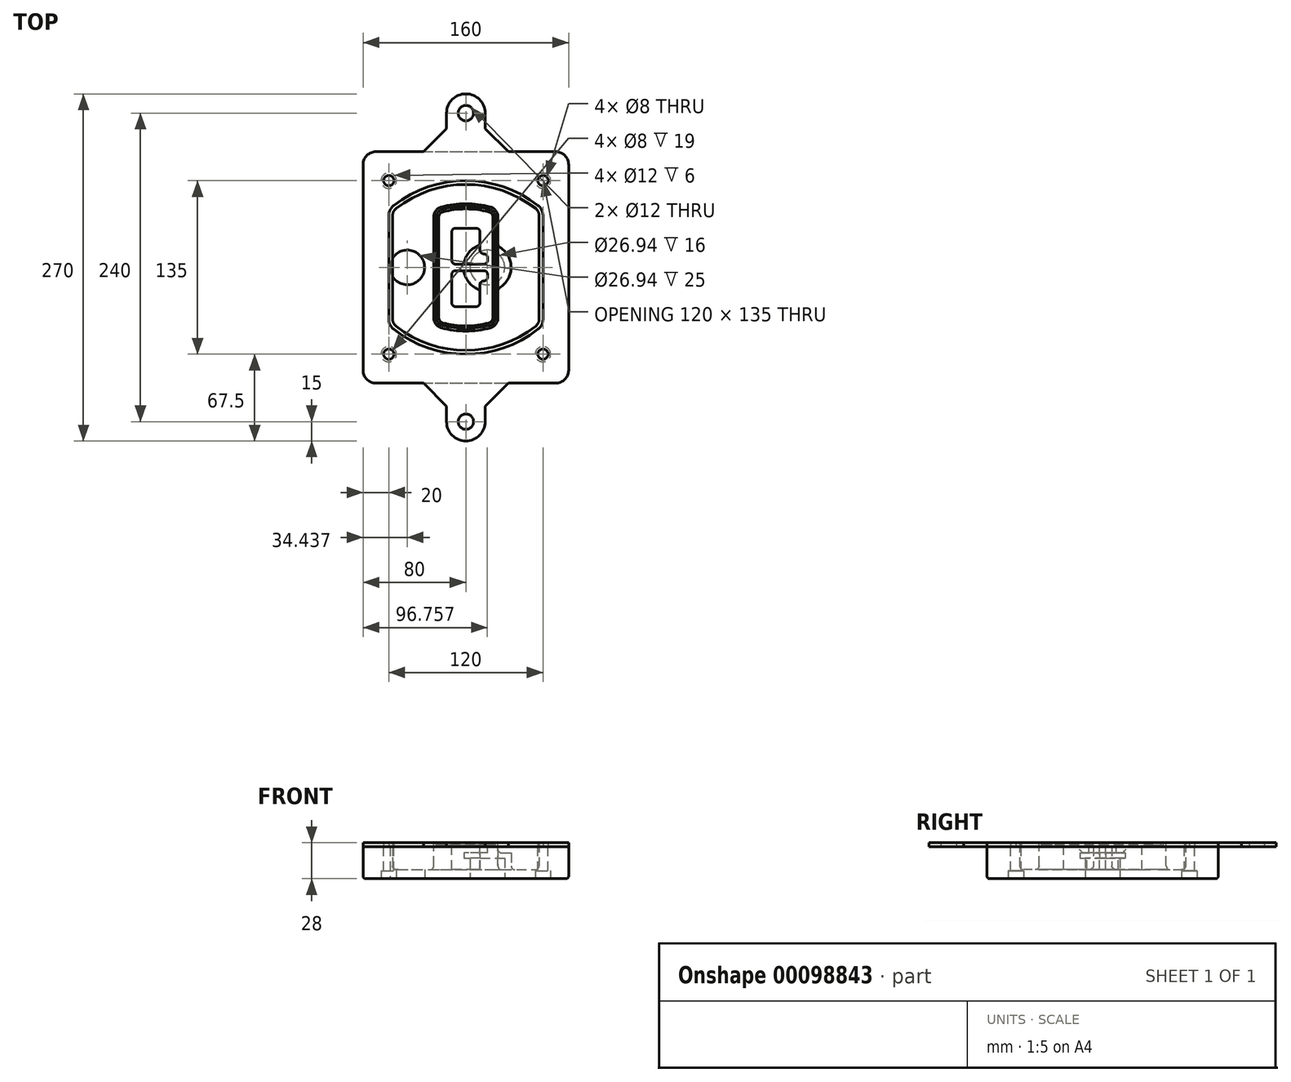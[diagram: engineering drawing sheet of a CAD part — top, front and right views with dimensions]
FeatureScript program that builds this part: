
annotation { "Feature Type Name" : "Feature", "Feature Type Description" : "" }
export const myFeature = defineFeature(function(context is Context, id is Id, definition is map)
    precondition{}
    {
        {
            var Q0;
            Q0=qCreatedBy(makeId("Top.planeOp"),FACE);
            var sketch = newSketch(context, id + "F0", { "sketchPlane" : qUnion([Q0])});
            skPoint(sketch, "E0.rect.middle", {"position": v(0, 0) * mm});
            skLineSegment(sketch, "E1.bottom", {"start": v(-70, -90) * mm, "end": v(70, -90) * mm});
            skLineSegment(sketch, "E1.top", {"start": v(-70, 90) * mm, "end": v(70, 90) * mm});
            skLineSegment(sketch, "E1.left", {"start": v(-80, -80) * mm, "end": v(-80, 80) * mm});
            skLineSegment(sketch, "E1.right", {"start": v(80, -80) * mm, "end": v(80, 80) * mm});
            skLineSegment(sketch, "E2", {"start": v(-80, 90) * mm, "end": v(80, -90) * mm, "construction": true});
            skLineSegment(sketch, "E3", {"start": v(80, 90) * mm, "end": v(-80, -90) * mm, "construction": true});
            skCircle(sketch, "E4", {"center": v(-60, 67.5) * mm, "radius": 4 * mm});
            skCircle(sketch, "E5", {"center": v(60, 67.5) * mm, "radius": 4 * mm});
            skCircle(sketch, "E6", {"center": v(60, -67.5) * mm, "radius": 4 * mm});
            skCircle(sketch, "E7", {"center": v(-60, -67.5) * mm, "radius": 4 * mm});
            skLineSegment(sketch, "E8", {"start": v(-60, 67.5) * mm, "end": v(60, 67.5) * mm, "construction": true});
            skLineSegment(sketch, "E9", {"start": v(60, 67.5) * mm, "end": v(60, -67.5) * mm, "construction": true});
            skLineSegment(sketch, "E10", {"start": v(60, -67.5) * mm, "end": v(-60, -67.5) * mm, "construction": true});
            skLineSegment(sketch, "E11", {"start": v(-60, -67.5) * mm, "end": v(-60, 67.5) * mm, "construction": true});
            skLineSegment(sketch, "E12", {"start": v(-60, 40.3) * mm, "end": v(-60, -40.3) * mm});
            skLineSegment(sketch, "E13", {"start": v(60, 40.3) * mm, "end": v(60, -40.3) * mm});
            skArc(sketch, "E14", {"start": v(56.15, 48.18) * mm, "mid": v(0, 67.5) * mm, "end": v(-56.15, 48.18) * mm});
            skArc(sketch, "E15", {"start": v(-56.15, -48.18) * mm, "mid": v(0, -67.5) * mm, "end": v(56.15, -48.18) * mm});
            skLineSegment(sketch, "E16", {"start": v(-60, 0) * mm, "end": v(60, 0) * mm, "construction": true});
            skPoint(sketch, "E17.visualSharp", {"position": v(-60, -45) * mm});
            skArc(sketch, "E17.filletArc", {"start": v(-60, -40.3) * mm, "mid": v(-58.99, -44.68) * mm, "end": v(-56.15, -48.18) * mm});
            skPoint(sketch, "E18.visualSharp", {"position": v(-60, 45) * mm});
            skArc(sketch, "E18.filletArc", {"start": v(-56.15, 48.18) * mm, "mid": v(-58.99, 44.68) * mm, "end": v(-60, 40.3) * mm});
            skPoint(sketch, "E19.visualSharp", {"position": v(60, 45) * mm});
            skArc(sketch, "E19.filletArc", {"start": v(60, 40.3) * mm, "mid": v(58.99, 44.68) * mm, "end": v(56.15, 48.18) * mm});
            skPoint(sketch, "E20.visualSharp", {"position": v(60, -45) * mm});
            skArc(sketch, "E20.filletArc", {"start": v(56.15, -48.18) * mm, "mid": v(58.99, -44.68) * mm, "end": v(60, -40.3) * mm});
            skPoint(sketch, "E21.visualSharp", {"position": v(-80, 90) * mm});
            skArc(sketch, "E21.filletArc", {"start": v(-70, 90) * mm, "mid": v(-77.07, 87.07) * mm, "end": v(-80, 80) * mm});
            skPoint(sketch, "E22.visualSharp", {"position": v(80, 90) * mm});
            skArc(sketch, "E22.filletArc", {"start": v(80, 80) * mm, "mid": v(77.07, 87.07) * mm, "end": v(70, 90) * mm});
            skPoint(sketch, "E23.visualSharp", {"position": v(80, -90) * mm});
            skArc(sketch, "E23.filletArc", {"start": v(70, -90) * mm, "mid": v(77.07, -87.07) * mm, "end": v(80, -80) * mm});
            skPoint(sketch, "E24.visualSharp", {"position": v(-80, -90) * mm});
            skArc(sketch, "E24.filletArc", {"start": v(-80, -80) * mm, "mid": v(-77.07, -87.07) * mm, "end": v(-70, -90) * mm});
            skArc(sketch, "E25.0", {"start": v(57, 40.3) * mm, "mid": v(56.3, 43.36) * mm, "end": v(54.3, 45.81) * mm});
            skLineSegment(sketch, "E25.1", {"start": v(57, 40.3) * mm, "end": v(57, -40.3) * mm});
            skArc(sketch, "E25.2", {"start": v(54.3, -45.81) * mm, "mid": v(56.3, -43.36) * mm, "end": v(57, -40.3) * mm});
            skArc(sketch, "E25.3", {"start": v(-54.3, -45.81) * mm, "mid": v(0, -64.5) * mm, "end": v(54.3, -45.81) * mm});
            skArc(sketch, "E25.4", {"start": v(-57, -40.3) * mm, "mid": v(-56.3, -43.36) * mm, "end": v(-54.3, -45.81) * mm});
            skArc(sketch, "E25.5", {"start": v(54.3, 45.81) * mm, "mid": v(0, 64.5) * mm, "end": v(-54.3, 45.81) * mm});
            skLineSegment(sketch, "E25.6", {"start": v(-57, 40.3) * mm, "end": v(-57, -40.3) * mm});
            skArc(sketch, "E25.7", {"start": v(-54.3, 45.81) * mm, "mid": v(-56.3, 43.36) * mm, "end": v(-57, 40.3) * mm});
            skArc(sketch, "E26.0", {"start": v(-58.62, 51.33) * mm, "mid": v(-62.58, 46.43) * mm, "end": v(-64, 40.3) * mm});
            skArc(sketch, "E26.1", {"start": v(58.62, 51.33) * mm, "mid": v(0, 71.5) * mm, "end": v(-58.62, 51.33) * mm});
            skArc(sketch, "E26.2", {"start": v(64, 40.3) * mm, "mid": v(62.58, 46.43) * mm, "end": v(58.62, 51.33) * mm});
            skLineSegment(sketch, "E26.3", {"start": v(64, 40.3) * mm, "end": v(64, -40.3) * mm});
            skArc(sketch, "E26.4", {"start": v(58.62, -51.33) * mm, "mid": v(62.58, -46.43) * mm, "end": v(64, -40.3) * mm});
            skLineSegment(sketch, "E26.5", {"start": v(-64, 40.3) * mm, "end": v(-64, -40.3) * mm});
            skArc(sketch, "E26.6", {"start": v(-58.62, -51.33) * mm, "mid": v(0, -71.5) * mm, "end": v(58.62, -51.33) * mm});
            skArc(sketch, "E26.7", {"start": v(-64, -40.3) * mm, "mid": v(-62.58, -46.43) * mm, "end": v(-58.62, -51.33) * mm});
            skSolve(sketch);
        }
        {
            var Q0;
            Q0=makeQuery(id+"F0.imprint","IMPRINT",FACE,{"disambiguationData":[TD([[makeQuery(id+"F0.imprint","IMPRINT",EDGE,{"derivedFrom":sQuery(id+"F0.wireOp",EDGE,"E1.bottom")}),1.0]])]});
            var Q1;
            Q1=makeQuery(id+"F0.imprint","IMPRINT",FACE,{"disambiguationData":[TD([[makeQuery(id+"F0.imprint","IMPRINT",EDGE,{"derivedFrom":sQuery(id+"F0.wireOp",EDGE,"E12")}),1.0]])]});
            var Q2;
            Q2=makeQuery(id+"F0.imprint","IMPRINT",FACE,{"disambiguationData":[TD([[makeQuery(id+"F0.imprint","IMPRINT",EDGE,{"derivedFrom":sQuery(id+"F0.wireOp",EDGE,"E25.0")}),1.0]])]});
            var Q3;
            Q3=makeQuery(id+"F0.imprint","IMPRINT",FACE,{"disambiguationData":[TD([[makeQuery(id+"F0.imprint","IMPRINT",EDGE,{"derivedFrom":sQuery(id+"F0.wireOp",EDGE,"E12")}),-1.0]])]});
            extrude(context, id + "F1", {"entities" : qUnion([Q0, Q1, Q2, Q3]), "oppositeDirection" : true, "depth" : 25 * mm});
        }
        {
            var Q0;
            Q0=makeQuery(id+"F0.imprint","IMPRINT",FACE,{"disambiguationData":[TD([[makeQuery(id+"F0.imprint","IMPRINT",EDGE,{"derivedFrom":sQuery(id+"F0.wireOp",EDGE,"E12")}),1.0]])]});
            extrude(context, id + "F2", {"entities" : qUnion([Q0]), "operationType" : NewBodyOperationType.ADD, "depth" : 3 * mm});
        }
        {
            var Q0;
            Q0=makeQuery(id+"F0.imprint","IMPRINT",FACE,{"disambiguationData":[TD([[makeQuery(id+"F0.imprint","IMPRINT",EDGE,{"derivedFrom":sQuery(id+"F0.wireOp",EDGE,"E25.0")}),1.0]])]});
            extrude(context, id + "F3", {"entities" : qUnion([Q0]), "operationType" : NewBodyOperationType.REMOVE, "oppositeDirection" : true, "depth" : 18 * mm});
        }
        {
            var Q0;
            Q0=makeQuery(id+"F2.opExtrude","CAP_FACE",FACE,{"disambiguationData":[OSD([sQuery(id+"F0.wireOp",EDGE,"E12"),sQuery(id+"F0.wireOp",EDGE,"E13"),sQuery(id+"F0.wireOp",EDGE,"E14"),sQuery(id+"F0.wireOp",EDGE,"E15"),sQuery(id+"F0.wireOp",EDGE,"E17.filletArc"),sQuery(id+"F0.wireOp",EDGE,"E18.filletArc"),sQuery(id+"F0.wireOp",EDGE,"E19.filletArc"),sQuery(id+"F0.wireOp",EDGE,"E20.filletArc"),sQuery(id+"F0.wireOp",EDGE,"E25.0"),sQuery(id+"F0.wireOp",EDGE,"E25.1"),sQuery(id+"F0.wireOp",EDGE,"E25.2"),sQuery(id+"F0.wireOp",EDGE,"E25.3"),sQuery(id+"F0.wireOp",EDGE,"E25.4"),sQuery(id+"F0.wireOp",EDGE,"E25.5"),sQuery(id+"F0.wireOp",EDGE,"E25.6"),sQuery(id+"F0.wireOp",EDGE,"E25.7")])],"isStart":false});
            var sketch = newSketch(context, id + "F4", { "sketchPlane" : qUnion([Q0])});
            skArc(sketch, "E27.0", {"start": v(-19.08, -46.97) * mm, "mid": v(0, -49.5) * mm, "end": v(19.08, -46.97) * mm});
            skArc(sketch, "E28.0", {"start": v(19.08, 46.97) * mm, "mid": v(0, 49.5) * mm, "end": v(-19.08, 46.97) * mm});
            skLineSegment(sketch, "E29", {"start": v(-25, 39.25) * mm, "end": v(-25, -39.25) * mm});
            skLineSegment(sketch, "E30", {"start": v(25, 39.25) * mm, "end": v(25, -39.25) * mm});
            skLineSegment(sketch, "E31", {"start": v(-25, 45.1) * mm, "end": v(25, 45.1) * mm, "construction": true});
            skLineSegment(sketch, "E32", {"start": v(-25, -45.1) * mm, "end": v(25, -45.1) * mm, "construction": true});
            skPoint(sketch, "E33.visualSharp", {"position": v(-25, 45.1) * mm});
            skArc(sketch, "E33.filletArc", {"start": v(-19.08, 46.97) * mm, "mid": v(-23.35, 44.11) * mm, "end": v(-25, 39.25) * mm});
            skPoint(sketch, "E34.visualSharp", {"position": v(25, 45.1) * mm});
            skArc(sketch, "E34.filletArc", {"start": v(25, 39.25) * mm, "mid": v(23.35, 44.11) * mm, "end": v(19.08, 46.97) * mm});
            skPoint(sketch, "E35.visualSharp", {"position": v(25, -45.1) * mm});
            skArc(sketch, "E35.filletArc", {"start": v(19.08, -46.97) * mm, "mid": v(23.35, -44.11) * mm, "end": v(25, -39.25) * mm});
            skPoint(sketch, "E36.visualSharp", {"position": v(-25, -45.1) * mm});
            skArc(sketch, "E36.filletArc", {"start": v(-25, -39.25) * mm, "mid": v(-23.35, -44.11) * mm, "end": v(-19.08, -46.97) * mm});
            skArc(sketch, "E37.0", {"start": v(54.3, 45.81) * mm, "mid": v(0, 64.5) * mm, "end": v(-54.3, 45.81) * mm});
            skArc(sketch, "E37.1", {"start": v(-54.3, 45.81) * mm, "mid": v(-56.3, 43.36) * mm, "end": v(-57, 40.3) * mm});
            skLineSegment(sketch, "E37.2", {"start": v(-57, 40.3) * mm, "end": v(-57, -40.3) * mm});
            skArc(sketch, "E37.3", {"start": v(-57, -40.3) * mm, "mid": v(-56.3, -43.36) * mm, "end": v(-54.3, -45.81) * mm});
            skArc(sketch, "E37.4", {"start": v(-54.3, -45.81) * mm, "mid": v(0, -64.5) * mm, "end": v(54.3, -45.81) * mm});
            skArc(sketch, "E37.5", {"start": v(54.3, -45.81) * mm, "mid": v(56.3, -43.36) * mm, "end": v(57, -40.3) * mm});
            skLineSegment(sketch, "E37.6", {"start": v(57, 40.3) * mm, "end": v(57, -40.3) * mm});
            skArc(sketch, "E37.7", {"start": v(57, 40.3) * mm, "mid": v(56.3, 43.36) * mm, "end": v(54.3, 45.81) * mm});
            skLineSegment(sketch, "E38.0", {"start": v(23, 39.25) * mm, "end": v(23, -39.25) * mm});
            skArc(sketch, "E38.1", {"start": v(18.56, -45.04) * mm, "mid": v(21.76, -42.9) * mm, "end": v(23, -39.25) * mm});
            skArc(sketch, "E38.2", {"start": v(-18.56, -45.04) * mm, "mid": v(0, -47.5) * mm, "end": v(18.56, -45.04) * mm});
            skArc(sketch, "E38.3", {"start": v(-23, -39.25) * mm, "mid": v(-21.76, -42.9) * mm, "end": v(-18.56, -45.04) * mm});
            skLineSegment(sketch, "E38.4", {"start": v(-23, 39.25) * mm, "end": v(-23, -39.25) * mm});
            skArc(sketch, "E38.5", {"start": v(23, 39.25) * mm, "mid": v(21.76, 42.9) * mm, "end": v(18.56, 45.04) * mm});
            skArc(sketch, "E38.6", {"start": v(-18.56, 45.04) * mm, "mid": v(-21.76, 42.9) * mm, "end": v(-23, 39.25) * mm});
            skArc(sketch, "E38.7", {"start": v(18.56, 45.04) * mm, "mid": v(0, 47.5) * mm, "end": v(-18.56, 45.04) * mm});
            skArc(sketch, "E39.0", {"start": v(21, 39.25) * mm, "mid": v(20.18, 41.68) * mm, "end": v(18.04, 43.1) * mm});
            skLineSegment(sketch, "E39.1", {"start": v(21, 39.25) * mm, "end": v(21, -39.25) * mm});
            skArc(sketch, "E39.2", {"start": v(18.04, -43.1) * mm, "mid": v(20.18, -41.68) * mm, "end": v(21, -39.25) * mm});
            skArc(sketch, "E39.3", {"start": v(-18.04, -43.1) * mm, "mid": v(0, -45.5) * mm, "end": v(18.04, -43.1) * mm});
            skArc(sketch, "E39.4", {"start": v(-21, -39.25) * mm, "mid": v(-20.18, -41.68) * mm, "end": v(-18.04, -43.1) * mm});
            skArc(sketch, "E39.5", {"start": v(18.04, 43.1) * mm, "mid": v(0, 45.5) * mm, "end": v(-18.04, 43.1) * mm});
            skLineSegment(sketch, "E39.6", {"start": v(-21, 39.25) * mm, "end": v(-21, -39.25) * mm});
            skArc(sketch, "E39.7", {"start": v(-18.04, 43.1) * mm, "mid": v(-20.18, 41.68) * mm, "end": v(-21, 39.25) * mm});
            skLineSegment(sketch, "E40", {"start": v(-25, 0) * mm, "end": v(25, 0) * mm, "construction": true});
            skLineSegment(sketch, "E41", {"start": v(-11, 5.5) * mm, "end": v(-11, 27.5) * mm});
            skLineSegment(sketch, "E42", {"start": v(-8, 30.5) * mm, "end": v(8, 30.5) * mm});
            skLineSegment(sketch, "E43", {"start": v(11, 27.5) * mm, "end": v(11, 13.5) * mm});
            skLineSegment(sketch, "E44", {"start": v(14, 10.5) * mm, "end": v(14, 10.5) * mm});
            skLineSegment(sketch, "E45", {"start": v(17, 7.5) * mm, "end": v(17, 5.5) * mm});
            skLineSegment(sketch, "E46", {"start": v(14, 2.5) * mm, "end": v(-8, 2.5) * mm});
            skPoint(sketch, "E47.visualSharp", {"position": v(-11, 30.5) * mm});
            skArc(sketch, "E47.filletArc", {"start": v(-8, 30.5) * mm, "mid": v(-10.12, 29.62) * mm, "end": v(-11, 27.5) * mm});
            skPoint(sketch, "E48.visualSharp", {"position": v(11, 30.5) * mm});
            skArc(sketch, "E48.filletArc", {"start": v(11, 27.5) * mm, "mid": v(10.12, 29.62) * mm, "end": v(8, 30.5) * mm});
            skPoint(sketch, "E49.visualSharp", {"position": v(11, 10.5) * mm});
            skArc(sketch, "E49.filletArc", {"start": v(11, 13.5) * mm, "mid": v(11.88, 11.38) * mm, "end": v(14, 10.5) * mm});
            skPoint(sketch, "E50.visualSharp", {"position": v(17, 10.5) * mm});
            skArc(sketch, "E50.filletArc", {"start": v(17, 7.5) * mm, "mid": v(16.12, 9.62) * mm, "end": v(14, 10.5) * mm});
            skPoint(sketch, "E51.visualSharp", {"position": v(17, 2.5) * mm});
            skArc(sketch, "E51.filletArc", {"start": v(14, 2.5) * mm, "mid": v(16.12, 3.38) * mm, "end": v(17, 5.5) * mm});
            skPoint(sketch, "E52.visualSharp", {"position": v(-11, 2.5) * mm});
            skArc(sketch, "E52.filletArc", {"start": v(-11, 5.5) * mm, "mid": v(-10.12, 3.38) * mm, "end": v(-8, 2.5) * mm});
            skLineSegment(sketch, "E53.0.MirrorCS", {"start": v(14, -2.5) * mm, "end": v(-8, -2.5) * mm});
            skArc(sketch, "E54.0.MirrorCS", {"start": v(-11, -5.5) * mm, "mid": v(-10.12, -3.38) * mm, "end": v(-8, -2.5) * mm});
            skLineSegment(sketch, "E55.0.MirrorCS", {"start": v(-11, -5.5) * mm, "end": v(-11, -27.5) * mm});
            skArc(sketch, "E56.0.MirrorCS", {"start": v(-8, -30.5) * mm, "mid": v(-10.12, -29.62) * mm, "end": v(-11, -27.5) * mm});
            skLineSegment(sketch, "E57.0.MirrorCS", {"start": v(-8, -30.5) * mm, "end": v(8, -30.5) * mm});
            skArc(sketch, "E58.0.MirrorCS", {"start": v(11, -27.5) * mm, "mid": v(10.12, -29.62) * mm, "end": v(8, -30.5) * mm});
            skLineSegment(sketch, "E59.0.MirrorCS", {"start": v(11, -27.5) * mm, "end": v(11, -13.5) * mm});
            skArc(sketch, "E60.0.MirrorCS", {"start": v(11, -13.5) * mm, "mid": v(11.88, -11.38) * mm, "end": v(14, -10.5) * mm});
            skArc(sketch, "E61.0.MirrorCS", {"start": v(17, -7.5) * mm, "mid": v(16.12, -9.62) * mm, "end": v(14, -10.5) * mm});
            skLineSegment(sketch, "E62.0.MirrorCS", {"start": v(17, -7.5) * mm, "end": v(17, -5.5) * mm});
            skArc(sketch, "E63.0.MirrorCS", {"start": v(14, -2.5) * mm, "mid": v(16.12, -3.38) * mm, "end": v(17, -5.5) * mm});
            skSolve(sketch);
        }
        {
            var Q0;
            Q0=makeQuery(id+"F4.imprint","IMPRINT",FACE,{"disambiguationData":[TD([[makeQuery(id+"F4.imprint","IMPRINT",EDGE,{"derivedFrom":sQuery(id+"F4.wireOp",EDGE,"E27.0")}),1.0]])]});
            var Q1;
            Q1=makeQuery(id+"F4.imprint","IMPRINT",FACE,{"disambiguationData":[TD([[makeQuery(id+"F4.imprint","IMPRINT",EDGE,{"derivedFrom":sQuery(id+"F4.wireOp",EDGE,"E38.0")}),-1.0]])]});
            var Q2;
            Q2=makeQuery(id+"F4.imprint","IMPRINT",FACE,{"disambiguationData":[TD([[makeQuery(id+"F4.imprint","IMPRINT",EDGE,{"derivedFrom":sQuery(id+"F4.wireOp",EDGE,"E39.0")}),1.0]])]});
            extrude(context, id + "F5", {"entities" : qUnion([Q0, Q1, Q2]), "operationType" : NewBodyOperationType.ADD, "endBound" : BoundingType.UP_TO_NEXT, "oppositeDirection" : true, "depth" : 25 * mm});
        }
        {
            var Q0;
            Q0=makeQuery(id+"F4.imprint","IMPRINT",FACE,{"disambiguationData":[TD([[makeQuery(id+"F4.imprint","IMPRINT",EDGE,{"derivedFrom":sQuery(id+"F4.wireOp",EDGE,"E38.0")}),-1.0]])]});
            extrude(context, id + "F6", {"entities" : qUnion([Q0]), "operationType" : NewBodyOperationType.REMOVE, "oppositeDirection" : true, "depth" : 2 * mm});
        }
        {
            var Q0;
            Q0=makeQuery(id+"F1.opExtrude","CAP_FACE",FACE,{"disambiguationData":[OSD([sQuery(id+"F0.wireOp",EDGE,"E1.bottom"),sQuery(id+"F0.wireOp",EDGE,"E1.top"),sQuery(id+"F0.wireOp",EDGE,"E1.left"),sQuery(id+"F0.wireOp",EDGE,"E1.right"),sQuery(id+"F0.wireOp",EDGE,"E4"),sQuery(id+"F0.wireOp",EDGE,"E5"),sQuery(id+"F0.wireOp",EDGE,"E6"),sQuery(id+"F0.wireOp",EDGE,"E7"),sQuery(id+"F0.wireOp",EDGE,"E21.filletArc"),sQuery(id+"F0.wireOp",EDGE,"E22.filletArc"),sQuery(id+"F0.wireOp",EDGE,"E23.filletArc"),sQuery(id+"F0.wireOp",EDGE,"E24.filletArc")])],"isStart":false});
            var sketch = newSketch(context, id + "F7", { "sketchPlane" : qUnion([Q0])});
            skCircle(sketch, "E64", {"center": v(16.76, 0) * mm, "radius": 13.47 * mm});
            skCircle(sketch, "E65", {"center": v(-45.56, 0) * mm, "radius": 13.47 * mm});
            skLineSegment(sketch, "E66", {"start": v(80, 0) * mm, "end": v(-80, 0) * mm});
            skCircle(sketch, "E67", {"center": v(16.76, 0) * mm, "radius": 18.47 * mm});
            skCircle(sketch, "E68", {"center": v(60, -67.5) * mm, "radius": 6 * mm});
            skCircle(sketch, "E69", {"center": v(-60, -67.5) * mm, "radius": 6 * mm});
            skCircle(sketch, "E70", {"center": v(-60, 67.5) * mm, "radius": 6 * mm});
            skCircle(sketch, "E71", {"center": v(60, 67.5) * mm, "radius": 6 * mm});
            skSolve(sketch);
        }
        {
            var Q0;
            {var subQ1=sQuery(id+"F7.wireOp",EDGE,"E66");var subQ4=sQuery(id+"F7.wireOp",EDGE,"E64");var subQ6=makeQuery(id+"F7.imprint","INTERSECT",VERTEX,{"disambiguationData":[OD(0.0)],"derivedFrom":[subQ4,subQ1]});Q0=makeQuery(id+"F7.imprint","IMPRINT",FACE,{"disambiguationData":[TD([[makeQuery(id+"F7.imprint","IMPRINT",EDGE,{"disambiguationData":[TD([[subQ6,-1.0]])],"derivedFrom":subQ4}),-1.0]])]});}
            var Q1;
            {var subQ0=sQuery(id+"F7.wireOp",EDGE,"E66");var subQ1=sQuery(id+"F7.wireOp",EDGE,"E64");var subQ3=makeQuery(id+"F7.imprint","INTERSECT",VERTEX,{"disambiguationData":[OD(0.0)],"derivedFrom":[subQ1,subQ0]});Q1=makeQuery(id+"F7.imprint","IMPRINT",FACE,{"disambiguationData":[TD([[makeQuery(id+"F7.imprint","IMPRINT",EDGE,{"disambiguationData":[TD([[subQ3,-1.0]])],"derivedFrom":subQ1}),1.0]])]});}
            var Q2;
            {var subQ0=sQuery(id+"F7.wireOp",EDGE,"E66");var subQ1=sQuery(id+"F7.wireOp",EDGE,"E64");var subQ3=makeQuery(id+"F7.imprint","INTERSECT",VERTEX,{"disambiguationData":[OD(0.0)],"derivedFrom":[subQ1,subQ0]});Q2=makeQuery(id+"F7.imprint","IMPRINT",FACE,{"disambiguationData":[TD([[makeQuery(id+"F7.imprint","IMPRINT",EDGE,{"disambiguationData":[TD([[subQ3,1.0]])],"derivedFrom":subQ1}),1.0]])]});}
            var Q3;
            {var subQ1=sQuery(id+"F7.wireOp",EDGE,"E66");var subQ4=sQuery(id+"F7.wireOp",EDGE,"E64");var subQ6=makeQuery(id+"F7.imprint","INTERSECT",VERTEX,{"disambiguationData":[OD(0.0)],"derivedFrom":[subQ4,subQ1]});Q3=makeQuery(id+"F7.imprint","IMPRINT",FACE,{"disambiguationData":[TD([[makeQuery(id+"F7.imprint","IMPRINT",EDGE,{"disambiguationData":[TD([[subQ6,1.0]])],"derivedFrom":subQ4}),-1.0]])]});}
            extrude(context, id + "F8", {"entities" : qUnion([Q0, Q1, Q2, Q3]), "operationType" : NewBodyOperationType.ADD, "oppositeDirection" : true, "depth" : 20 * mm});
        }
        {
            var Q0;
            {var subQ0=sQuery(id+"F7.wireOp",EDGE,"E66");var subQ1=sQuery(id+"F7.wireOp",EDGE,"E64");var subQ3=makeQuery(id+"F7.imprint","INTERSECT",VERTEX,{"disambiguationData":[OD(0.0)],"derivedFrom":[subQ1,subQ0]});Q0=makeQuery(id+"F7.imprint","IMPRINT",FACE,{"disambiguationData":[TD([[makeQuery(id+"F7.imprint","IMPRINT",EDGE,{"disambiguationData":[TD([[subQ3,-1.0]])],"derivedFrom":subQ1}),1.0]])]});}
            var Q1;
            {var subQ0=sQuery(id+"F7.wireOp",EDGE,"E66");var subQ1=sQuery(id+"F7.wireOp",EDGE,"E64");var subQ3=makeQuery(id+"F7.imprint","INTERSECT",VERTEX,{"disambiguationData":[OD(0.0)],"derivedFrom":[subQ1,subQ0]});Q1=makeQuery(id+"F7.imprint","IMPRINT",FACE,{"disambiguationData":[TD([[makeQuery(id+"F7.imprint","IMPRINT",EDGE,{"disambiguationData":[TD([[subQ3,1.0]])],"derivedFrom":subQ1}),1.0]])]});}
            extrude(context, id + "F9", {"entities" : qUnion([Q0, Q1]), "operationType" : NewBodyOperationType.REMOVE, "oppositeDirection" : true, "depth" : 16 * mm});
        }
        {
            var Q0;
            {var subQ0=sQuery(id+"F7.wireOp",EDGE,"E66");var subQ1=sQuery(id+"F7.wireOp",EDGE,"E65");var subQ3=makeQuery(id+"F7.imprint","INTERSECT",VERTEX,{"disambiguationData":[OD(0.0)],"derivedFrom":[subQ1,subQ0]});Q0=makeQuery(id+"F7.imprint","IMPRINT",FACE,{"disambiguationData":[TD([[makeQuery(id+"F7.imprint","IMPRINT",EDGE,{"disambiguationData":[TD([[subQ3,-1.0]])],"derivedFrom":subQ1}),1.0]])]});}
            var Q1;
            {var subQ0=sQuery(id+"F7.wireOp",EDGE,"E66");var subQ1=sQuery(id+"F7.wireOp",EDGE,"E65");var subQ3=makeQuery(id+"F7.imprint","INTERSECT",VERTEX,{"disambiguationData":[OD(0.0)],"derivedFrom":[subQ1,subQ0]});Q1=makeQuery(id+"F7.imprint","IMPRINT",FACE,{"disambiguationData":[TD([[makeQuery(id+"F7.imprint","IMPRINT",EDGE,{"disambiguationData":[TD([[subQ3,1.0]])],"derivedFrom":subQ1}),1.0]])]});}
            extrude(context, id + "F10", {"entities" : qUnion([Q0, Q1]), "operationType" : NewBodyOperationType.REMOVE, "oppositeDirection" : true, "depth" : 25 * mm});
        }
        {
            var Q0;
            Q0=makeQuery(id+"F7.imprint","IMPRINT",FACE,{"disambiguationData":[TD([[makeQuery(id+"F7.imprint","IMPRINT",EDGE,{"derivedFrom":sQuery(id+"F7.wireOp",EDGE,"E68")}),1.0]])]});
            var Q1;
            Q1=makeQuery(id+"F7.imprint","IMPRINT",FACE,{"disambiguationData":[TD([[makeQuery(id+"F7.imprint","IMPRINT",EDGE,{"derivedFrom":makeQuery(id+"F1.opExtrude","CAP_EDGE",EDGE,{"disambiguationData":[OSD([sQuery(id+"F0.wireOp",EDGE,"E5")])],"isStart":false})}),-1.0]])]});
            var Q2;
            Q2=makeQuery(id+"F7.imprint","IMPRINT",FACE,{"disambiguationData":[TD([[makeQuery(id+"F7.imprint","IMPRINT",EDGE,{"derivedFrom":sQuery(id+"F7.wireOp",EDGE,"E69")}),1.0]])]});
            var Q3;
            Q3=makeQuery(id+"F7.imprint","IMPRINT",FACE,{"disambiguationData":[TD([[makeQuery(id+"F7.imprint","IMPRINT",EDGE,{"derivedFrom":makeQuery(id+"F1.opExtrude","CAP_EDGE",EDGE,{"disambiguationData":[OSD([sQuery(id+"F0.wireOp",EDGE,"E4")])],"isStart":false})}),-1.0]])]});
            var Q4;
            Q4=makeQuery(id+"F7.imprint","IMPRINT",FACE,{"disambiguationData":[TD([[makeQuery(id+"F7.imprint","IMPRINT",EDGE,{"derivedFrom":sQuery(id+"F7.wireOp",EDGE,"E70")}),1.0]])]});
            var Q5;
            Q5=makeQuery(id+"F7.imprint","IMPRINT",FACE,{"disambiguationData":[TD([[makeQuery(id+"F7.imprint","IMPRINT",EDGE,{"derivedFrom":makeQuery(id+"F1.opExtrude","CAP_EDGE",EDGE,{"disambiguationData":[OSD([sQuery(id+"F0.wireOp",EDGE,"E7")])],"isStart":false})}),-1.0]])]});
            var Q6;
            Q6=makeQuery(id+"F7.imprint","IMPRINT",FACE,{"disambiguationData":[TD([[makeQuery(id+"F7.imprint","IMPRINT",EDGE,{"derivedFrom":sQuery(id+"F7.wireOp",EDGE,"E71")}),1.0]])]});
            var Q7;
            Q7=makeQuery(id+"F7.imprint","IMPRINT",FACE,{"disambiguationData":[TD([[makeQuery(id+"F7.imprint","IMPRINT",EDGE,{"derivedFrom":makeQuery(id+"F1.opExtrude","CAP_EDGE",EDGE,{"disambiguationData":[OSD([sQuery(id+"F0.wireOp",EDGE,"E6")])],"isStart":false})}),-1.0]])]});
            extrude(context, id + "F11", {"entities" : qUnion([Q0, Q1, Q2, Q3, Q4, Q5, Q6, Q7]), "operationType" : NewBodyOperationType.REMOVE, "oppositeDirection" : true, "depth" : 6 * mm});
        }
        {
            var Q0;
            Q0=makeQuery(id+"F9.boolean.opBoolean","COPY",FACE,{"derivedFrom":makeQuery(id+"F9.opExtrude","CAP_FACE",FACE,{"disambiguationData":[OSD([sQuery(id+"F7.wireOp",EDGE,"E64")])],"isStart":false})});
            var sketch = newSketch(context, id + "F12", { "sketchPlane" : qUnion([Q0])});
            skArc(sketch, "E72.0", {"start": v(11, 17.55) * mm, "mid": v(2.57, 11.82) * mm, "end": v(-1.54, 2.5) * mm});
            skArc(sketch, "E72.1", {"start": v(-1.54, -2.5) * mm, "mid": v(2.57, -11.82) * mm, "end": v(11, -17.55) * mm});
            skLineSegment(sketch, "E73", {"start": v(-1.54, -2.5) * mm, "end": v(14, -2.5) * mm});
            skLineSegment(sketch, "E74.0", {"start": v(14, 2.5) * mm, "end": v(-1.54, 2.5) * mm});
            skArc(sketch, "E74.1", {"start": v(14, 2.5) * mm, "mid": v(16.12, 3.38) * mm, "end": v(17, 5.5) * mm});
            skLineSegment(sketch, "E74.2", {"start": v(17, 7.5) * mm, "end": v(17, 5.5) * mm});
            skArc(sketch, "E74.3", {"start": v(17, 7.5) * mm, "mid": v(16.12, 9.62) * mm, "end": v(14, 10.5) * mm});
            skArc(sketch, "E74.4", {"start": v(11, 13.5) * mm, "mid": v(11.88, 11.38) * mm, "end": v(14, 10.5) * mm});
            skLineSegment(sketch, "E74.5", {"start": v(11, 17.55) * mm, "end": v(11, 13.5) * mm});
            skLineSegment(sketch, "E74.7", {"start": v(14, -2.5) * mm, "end": v(-1.54, -2.5) * mm});
            skArc(sketch, "E74.8", {"start": v(14, -2.5) * mm, "mid": v(16.12, -3.38) * mm, "end": v(17, -5.5) * mm});
            skLineSegment(sketch, "E74.9", {"start": v(17, -7.5) * mm, "end": v(17, -5.5) * mm});
            skArc(sketch, "E74.10", {"start": v(17, -7.5) * mm, "mid": v(16.12, -9.62) * mm, "end": v(14, -10.5) * mm});
            skArc(sketch, "E74.11", {"start": v(11, -13.5) * mm, "mid": v(11.88, -11.38) * mm, "end": v(14, -10.5) * mm});
            skLineSegment(sketch, "E74.12", {"start": v(11, -17.55) * mm, "end": v(11, -13.5) * mm});
            skPoint(sketch, "E75.orphan", {"position": v(11, -27.5) * mm});
            skPoint(sketch, "E76.orphan", {"position": v(-8, -2.5) * mm});
            skPoint(sketch, "E77.orphan", {"position": v(-8, 2.5) * mm});
            skPoint(sketch, "E78.orphan", {"position": v(11, 27.5) * mm});
            skSolve(sketch);
        }
        {
            var Q0;
            {var subQ7=sQuery(id+"F12.wireOp",EDGE,"E72.0");var subQ14=sQuery(id+"F12.wireOp",EDGE,"E72.1");var subQ16=sQuery(id+"F12.wireOp",EDGE,"E74.1");var subQ18=sQuery(id+"F12.wireOp",EDGE,"E74.8");Q0=qUnion([makeQuery(id+"F12.imprint","IMPRINT",FACE,{"disambiguationData":[TD([[makeQuery(id+"F12.imprint","IMPRINT",EDGE,{"derivedFrom":subQ7}),1.0]])]}),makeQuery(id+"F12.imprint","IMPRINT",FACE,{"disambiguationData":[TD([[makeQuery(id+"F12.imprint","IMPRINT",EDGE,{"derivedFrom":subQ14}),1.0]])]}),makeQuery(id+"F12.imprint","IMPRINT",FACE,{"disambiguationData":[TD([[makeQuery(id+"F12.imprint","IMPRINT",EDGE,{"derivedFrom":subQ16}),1.0]])]}),makeQuery(id+"F12.imprint","IMPRINT",FACE,{"disambiguationData":[TD([[makeQuery(id+"F12.imprint","IMPRINT",EDGE,{"derivedFrom":subQ18}),-1.0]])]})]);}
            var Q1;
            Q1=makeQuery(id+"F5.boolean.opBoolean","SPLIT",FACE,{"disambiguationData":[TD([makeQuery(id+"F5.opExtrude","SWEPT_FACE",FACE,{"disambiguationData":[OSD([sQuery(id+"F4.wireOp",EDGE,"E41")])]})])],"derivedFrom":makeQuery(id+"F3.boolean.opBoolean","COPY",FACE,{"derivedFrom":makeQuery(id+"F3.opExtrude","CAP_FACE",FACE,{"disambiguationData":[OSD([sQuery(id+"F0.wireOp",EDGE,"E25.0"),sQuery(id+"F0.wireOp",EDGE,"E25.1"),sQuery(id+"F0.wireOp",EDGE,"E25.2"),sQuery(id+"F0.wireOp",EDGE,"E25.3"),sQuery(id+"F0.wireOp",EDGE,"E25.4"),sQuery(id+"F0.wireOp",EDGE,"E25.5"),sQuery(id+"F0.wireOp",EDGE,"E25.6"),sQuery(id+"F0.wireOp",EDGE,"E25.7")])],"isStart":false})})});
            extrude(context, id + "F13", {"entities" : qUnion([Q0]), "operationType" : NewBodyOperationType.REMOVE, "endBound" : BoundingType.UP_TO_SURFACE, "endBoundEntityFace" : qUnion([Q1]), "depth" : 25 * mm});
        }
        {
            var Q0;
            Q0=makeQuery(id+"F3.boolean.opBoolean","COPY",EDGE,{"derivedFrom":makeQuery(id+"F3.opExtrude","CAP_EDGE",EDGE,{"disambiguationData":[OSD([sQuery(id+"F0.wireOp",EDGE,"E25.6")])],"isStart":false})});
            var Q1;
            Q1=makeQuery(id+"F8.boolean.opBoolean","INTERSECT",EDGE,{"derivedFrom":[makeQuery(id+"F5.opExtrude","SWEPT_FACE",FACE,{"disambiguationData":[OSD([sQuery(id+"F4.wireOp",EDGE,"E30")])]}),makeQuery(id+"F8.opExtrude","CAP_FACE",FACE,{"disambiguationData":[OSD([sQuery(id+"F7.wireOp",EDGE,"E67")])],"isStart":false})]});
            var Q2;
            Q2=makeQuery(id+"F8.boolean.opBoolean","INTERSECT",EDGE,{"disambiguationData":[OD(1.0)],"derivedFrom":[makeQuery(id+"F5.opExtrude","SWEPT_FACE",FACE,{"disambiguationData":[OSD([sQuery(id+"F4.wireOp",EDGE,"E30")])]}),makeQuery(id+"F8.opExtrude","SWEPT_FACE",FACE,{"disambiguationData":[OSD([sQuery(id+"F7.wireOp",EDGE,"E67")])]})]});
            var Q3;
            {var subQ0=sQuery(id+"F4.wireOp",EDGE,"E30");Q3=makeQuery(id+"F8.boolean.opBoolean","SPLIT",EDGE,{"disambiguationData":[TD([makeQuery(id+"F5.opExtrude","SWEPT_FACE",FACE,{"disambiguationData":[OSD([sQuery(id+"F4.wireOp",EDGE,"E35.filletArc")])]})])],"derivedFrom":makeQuery(id+"F5.opExtrude","CAP_EDGE",EDGE,{"disambiguationData":[OSD([subQ0])],"isStart":false})});}
            var Q4;
            {var subQ0=sQuery(id+"F0.wireOp",EDGE,"E25.7");var subQ1=sQuery(id+"F0.wireOp",EDGE,"E25.1");var subQ2=sQuery(id+"F0.wireOp",EDGE,"E25.6");var subQ3=sQuery(id+"F0.wireOp",EDGE,"E25.5");var subQ4=sQuery(id+"F0.wireOp",EDGE,"E25.4");var subQ5=sQuery(id+"F0.wireOp",EDGE,"E25.0");var subQ6=sQuery(id+"F0.wireOp",EDGE,"E25.2");var subQ7=sQuery(id+"F0.wireOp",EDGE,"E25.3");Q4=makeQuery(id+"F8.boolean.opBoolean","INTERSECT",EDGE,{"derivedFrom":[makeQuery(id+"F5.boolean.opBoolean","SPLIT",FACE,{"disambiguationData":[TD([makeQuery(id+"F2.opExtrude","SWEPT_FACE",FACE,{"disambiguationData":[OSD([subQ5])]})])],"derivedFrom":makeQuery(id+"F3.boolean.opBoolean","COPY",FACE,{"derivedFrom":makeQuery(id+"F3.opExtrude","CAP_FACE",FACE,{"disambiguationData":[OSD([subQ5,subQ1,subQ6,subQ7,subQ4,subQ3,subQ2,subQ0])],"isStart":false})})}),makeQuery(id+"F8.opExtrude","SWEPT_FACE",FACE,{"disambiguationData":[OSD([sQuery(id+"F7.wireOp",EDGE,"E67")])]})]});}
            var Q5;
            Q5=makeQuery(id+"F8.boolean.opBoolean","INTERSECT",EDGE,{"disambiguationData":[OD(0.0)],"derivedFrom":[makeQuery(id+"F5.opExtrude","SWEPT_FACE",FACE,{"disambiguationData":[OSD([sQuery(id+"F4.wireOp",EDGE,"E30")])]}),makeQuery(id+"F8.opExtrude","SWEPT_FACE",FACE,{"disambiguationData":[OSD([sQuery(id+"F7.wireOp",EDGE,"E67")])]})]});
            fillet(context, id + "F14", {"entities" : qUnion([Q0, Q1, Q2, Q3, Q4, Q5]), "radius" : 3 * mm, "tangentPropagation" : true, "allowEdgeOverflow" : false});
        }
        {
            var Q0;
            Q0=makeQuery(id+"F1.opExtrude","CAP_EDGE",EDGE,{"disambiguationData":[OSD([sQuery(id+"F0.wireOp",EDGE,"E1.bottom")])],"isStart":false});
            fillet(context, id + "F15", {"entities" : qUnion([Q0]), "radius" : 2 * mm, "tangentPropagation" : true, "allowEdgeOverflow" : false});
        }
        {
            var Q0;
            {var subQ0=sQuery(id+"F0.wireOp",EDGE,"E22.filletArc");var subQ1=sQuery(id+"F0.wireOp",EDGE,"E7");var subQ2=sQuery(id+"F0.wireOp",EDGE,"E6");var subQ3=sQuery(id+"F0.wireOp",EDGE,"E5");var subQ4=sQuery(id+"F0.wireOp",EDGE,"E4");var subQ5=sQuery(id+"F0.wireOp",EDGE,"E1.bottom");var subQ6=sQuery(id+"F0.wireOp",EDGE,"E21.filletArc");var subQ7=sQuery(id+"F0.wireOp",EDGE,"E1.top");var subQ8=sQuery(id+"F0.wireOp",EDGE,"E1.left");var subQ9=sQuery(id+"F0.wireOp",EDGE,"E1.right");var subQ10=sQuery(id+"F0.wireOp",EDGE,"E23.filletArc");var subQ11=sQuery(id+"F0.wireOp",EDGE,"E24.filletArc");Q0=makeQuery(id+"F2.boolean.opBoolean","SPLIT",FACE,{"disambiguationData":[TD([makeQuery(id+"F1.opExtrude","SWEPT_FACE",FACE,{"disambiguationData":[OSD([subQ5])]})])],"derivedFrom":makeQuery(id+"F1.opExtrude","CAP_FACE",FACE,{"disambiguationData":[OSD([subQ5,subQ7,subQ8,subQ9,subQ4,subQ3,subQ2,subQ1,subQ6,subQ0,subQ10,subQ11])],"isStart":true})});}
            var sketch = newSketch(context, id + "F16", { "sketchPlane" : qUnion([Q0])});
            skLineSegment(sketch, "E79.0", {"start": v(-70, 90) * mm, "end": v(70, 90) * mm});
            skArc(sketch, "E79.1", {"start": v(80, 80) * mm, "mid": v(77.07, 87.07) * mm, "end": v(70, 90) * mm});
            skLineSegment(sketch, "E79.2", {"start": v(80, -80) * mm, "end": v(80, 80) * mm});
            skCircle(sketch, "E79.3", {"center": v(60, 67.5) * mm, "radius": 4 * mm});
            skArc(sketch, "E79.4", {"start": v(-70, 90) * mm, "mid": v(-77.07, 87.07) * mm, "end": v(-80, 80) * mm});
            skLineSegment(sketch, "E79.5", {"start": v(-80, -80) * mm, "end": v(-80, 80) * mm});
            skArc(sketch, "E79.6", {"start": v(-80, -80) * mm, "mid": v(-77.07, -87.07) * mm, "end": v(-70, -90) * mm});
            skLineSegment(sketch, "E79.7", {"start": v(-70, -90) * mm, "end": v(70, -90) * mm});
            skArc(sketch, "E79.8", {"start": v(70, -90) * mm, "mid": v(77.07, -87.07) * mm, "end": v(80, -80) * mm});
            skCircle(sketch, "E79.9", {"center": v(60, -67.5) * mm, "radius": 4 * mm});
            skCircle(sketch, "E79.10", {"center": v(-60, -67.5) * mm, "radius": 4 * mm});
            skCircle(sketch, "E79.11", {"center": v(-60, 67.5) * mm, "radius": 4 * mm});
            skArc(sketch, "E79.12", {"start": v(56.15, 48.18) * mm, "mid": v(0, 67.5) * mm, "end": v(-56.15, 48.18) * mm});
            skArc(sketch, "E79.13", {"start": v(60, 40.3) * mm, "mid": v(58.99, 44.68) * mm, "end": v(56.15, 48.18) * mm});
            skLineSegment(sketch, "E79.14", {"start": v(60, 40.3) * mm, "end": v(60, -40.3) * mm});
            skArc(sketch, "E79.15", {"start": v(-56.15, 48.18) * mm, "mid": v(-58.99, 44.68) * mm, "end": v(-60, 40.3) * mm});
            skLineSegment(sketch, "E79.16", {"start": v(-60, 40.3) * mm, "end": v(-60, -40.3) * mm});
            skArc(sketch, "E79.17", {"start": v(-60, -40.3) * mm, "mid": v(-58.99, -44.68) * mm, "end": v(-56.15, -48.18) * mm});
            skArc(sketch, "E79.18", {"start": v(-56.15, -48.18) * mm, "mid": v(0, -67.5) * mm, "end": v(56.15, -48.18) * mm});
            skArc(sketch, "E79.19", {"start": v(56.15, -48.18) * mm, "mid": v(58.99, -44.68) * mm, "end": v(60, -40.3) * mm});
            skLineSegment(sketch, "E80", {"start": v(0, 90) * mm, "end": v(0, 120) * mm, "construction": true});
            skPoint(sketch, "E80.endSnap0", {"position": v(0, 90) * mm});
            skCircle(sketch, "E81", {"center": v(0, 120) * mm, "radius": 6 * mm});
            skLineSegment(sketch, "E82", {"start": v(-33, 90) * mm, "end": v(-15, 108) * mm});
            skLineSegment(sketch, "E83", {"start": v(33, 90) * mm, "end": v(15, 108) * mm});
            skLineSegment(sketch, "E84", {"start": v(-15, 108) * mm, "end": v(-15, 120) * mm});
            skLineSegment(sketch, "E85", {"start": v(15, 108) * mm, "end": v(15, 120) * mm});
            skArc(sketch, "E86", {"start": v(15, 120) * mm, "mid": v(0, 135) * mm, "end": v(-15, 120) * mm});
            skLineSegment(sketch, "E87", {"start": v(-80, 0) * mm, "end": v(80, 0) * mm, "construction": true});
            skLineSegment(sketch, "E88.MirrorCS", {"start": v(-15, -108) * mm, "end": v(-15, -120) * mm});
            skCircle(sketch, "E89.MirrorC", {"center": v(0, -120) * mm, "radius": 6 * mm});
            skArc(sketch, "E90.MirrorCS", {"start": v(15, -120) * mm, "mid": v(0, -135) * mm, "end": v(-15, -120) * mm});
            skLineSegment(sketch, "E91.MirrorCS", {"start": v(15, -108) * mm, "end": v(15, -120) * mm});
            skLineSegment(sketch, "E92.MirrorCS", {"start": v(33, -90) * mm, "end": v(15, -108) * mm});
            skLineSegment(sketch, "E93.MirrorCS", {"start": v(0, -90) * mm, "end": v(0, -120) * mm, "construction": true});
            skLineSegment(sketch, "E94.MirrorCS", {"start": v(-33, -90) * mm, "end": v(-15, -108) * mm});
            skSolve(sketch);
        }
        {
            var Q0;
            Q0=makeQuery(id+"F16.imprint","IMPRINT",FACE,{"disambiguationData":[TD([[makeQuery(id+"F16.imprint","IMPRINT",EDGE,{"derivedFrom":sQuery(id+"F16.wireOp",EDGE,"E88.MirrorCS")}),1.0]])]});
            var Q1;
            Q1=makeQuery(id+"F16.imprint","IMPRINT",FACE,{"disambiguationData":[TD([[makeQuery(id+"F16.imprint","IMPRINT",EDGE,{"derivedFrom":sQuery(id+"F16.wireOp",EDGE,"E81")}),-1.0]])]});
            var Q2;
            {var subQ4=sQuery(id+"F16.wireOp",EDGE,"E79.1");Q2=makeQuery(id+"F16.imprint","IMPRINT",FACE,{"disambiguationData":[TD([[makeQuery(id+"F16.imprint","IMPRINT",EDGE,{"derivedFrom":subQ4}),1.0]])]});}
            var Q3;
            Q3=makeQuery(id+"F2.opExtrude","CAP_FACE",FACE,{"disambiguationData":[OSD([sQuery(id+"F0.wireOp",EDGE,"E12"),sQuery(id+"F0.wireOp",EDGE,"E13"),sQuery(id+"F0.wireOp",EDGE,"E14"),sQuery(id+"F0.wireOp",EDGE,"E15"),sQuery(id+"F0.wireOp",EDGE,"E17.filletArc"),sQuery(id+"F0.wireOp",EDGE,"E18.filletArc"),sQuery(id+"F0.wireOp",EDGE,"E19.filletArc"),sQuery(id+"F0.wireOp",EDGE,"E20.filletArc"),sQuery(id+"F0.wireOp",EDGE,"E25.0"),sQuery(id+"F0.wireOp",EDGE,"E25.1"),sQuery(id+"F0.wireOp",EDGE,"E25.2"),sQuery(id+"F0.wireOp",EDGE,"E25.3"),sQuery(id+"F0.wireOp",EDGE,"E25.4"),sQuery(id+"F0.wireOp",EDGE,"E25.5"),sQuery(id+"F0.wireOp",EDGE,"E25.6"),sQuery(id+"F0.wireOp",EDGE,"E25.7")])],"isStart":false});
            extrude(context, id + "F17", {"entities" : qUnion([Q0, Q1, Q2]), "endBound" : BoundingType.UP_TO_SURFACE, "endBoundEntityFace" : qUnion([Q3]), "depth" : 25 * mm});
        }
    });
